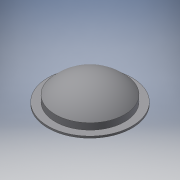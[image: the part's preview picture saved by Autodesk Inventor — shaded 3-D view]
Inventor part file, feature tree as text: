
AUTODESK INVENTOR PART (.ipt)
format: ipt  version: 2016 SP2 (Build 200236200, 236)  size: 139,264 bytes
history: native  units: mm
features: revolve x1, sketch x1, reference x1
ambient origin geometry x8: Origin, YZ Plane, XZ Plane, XY Plane, X Axis, Y Axis, Z Axis, Center Point
bodies: Volumenkörper1 (feature_tree)
feature tree (3):
  revolve  "Umdrehung1"
  sketch  "Skizze1"  dims[d0=2.0mm d1=7.0mm d2=8.0mm d3=46.0mm d4=0.5mm d5=0.5mm d7=50.0mm d8=9.0mm d9=4.0mm d10=42.760567mm d11=26.503846mm]
  reference  "Referenz1"
